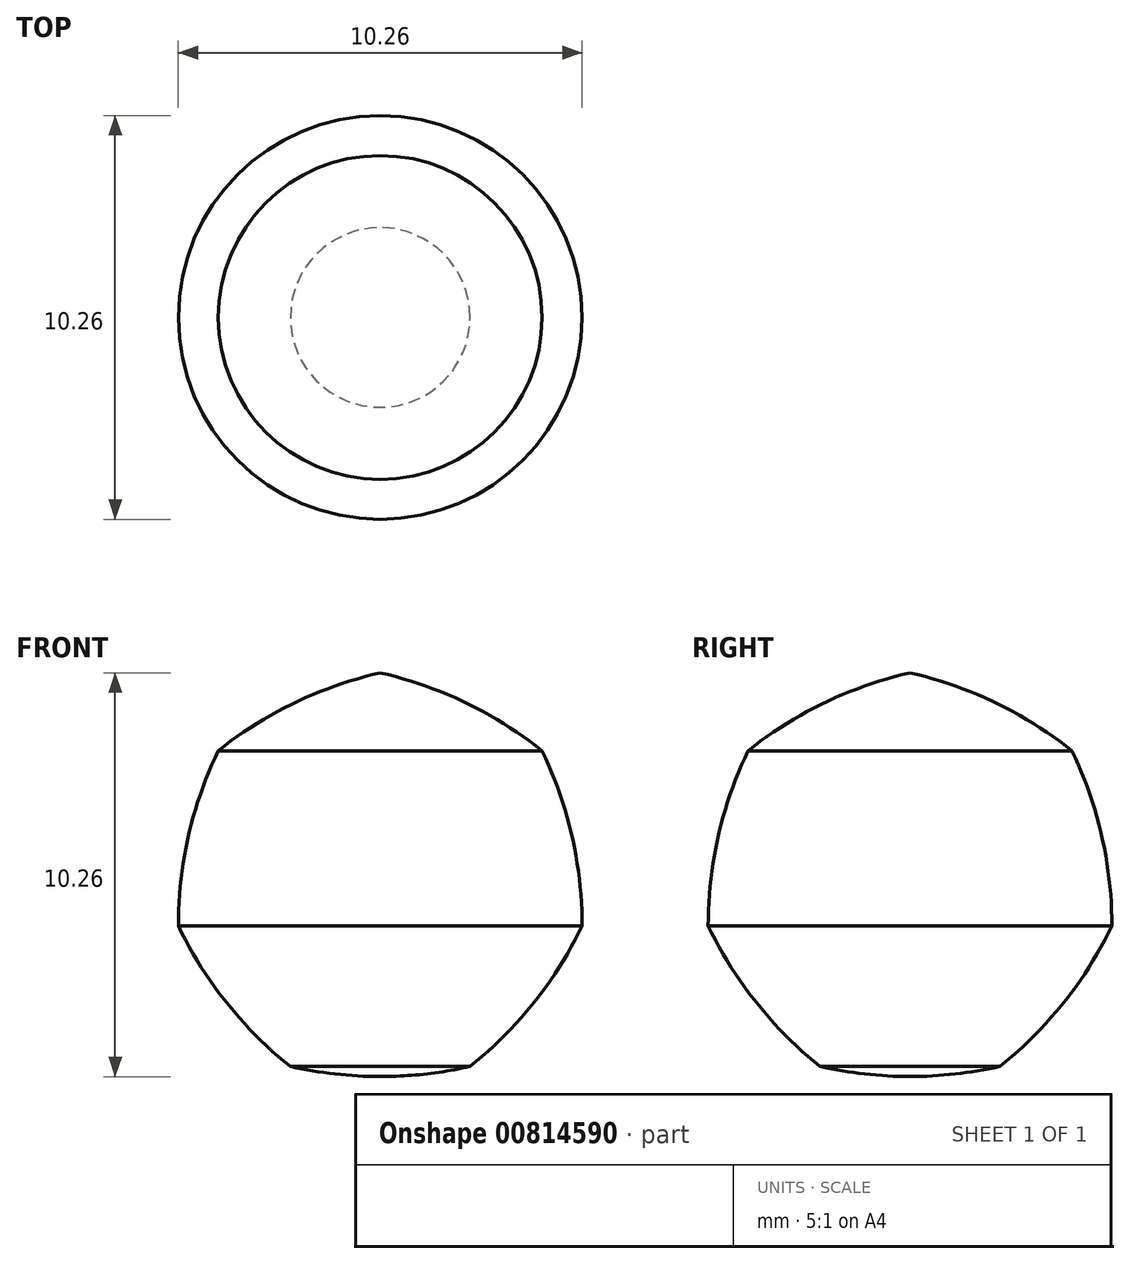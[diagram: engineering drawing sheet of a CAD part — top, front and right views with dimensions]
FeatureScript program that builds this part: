
annotation { "Feature Type Name" : "Feature", "Feature Type Description" : "" }
export const myFeature = defineFeature(function(context is Context, id is Id, definition is map)
    precondition{}
    {
        {
            var Q0;
            Q0=qCreatedBy(makeId("Front.planeOp"),FACE);
            var sketch = newSketch(context, id + "F0", { "sketchPlane" : qUnion([Q0])});
            skArc(sketch, "E0.cCircle", {"start": v(0, -4.74) * mm, "mid": v(4.74, 0) * mm, "end": v(0, 4.74) * mm, "construction": true});
            skLineSegment(sketch, "E0.0", {"start": v(2.28, -4.74) * mm, "end": v(0, -4.74) * mm});
            skLineSegment(sketch, "E0.4", {"start": v(0, 5.26) * mm, "end": v(4.11, 3.28) * mm});
            skLineSegment(sketch, "E0.5", {"start": v(4.11, 3.28) * mm, "end": v(5.13, -1.17) * mm});
            skLineSegment(sketch, "E0.6", {"start": v(5.13, -1.17) * mm, "end": v(2.28, -4.74) * mm});
            skPoint(sketch, "E0.0.midPoint", {"position": v(0, -4.74) * mm});
            skArc(sketch, "E1", {"start": v(0, -5) * mm, "mid": v(1.15, -4.93) * mm, "end": v(2.28, -4.74) * mm});
            skArc(sketch, "E2.trimOffspring", {"start": v(4.11, 3.28) * mm, "mid": v(2.17, 4.5) * mm, "end": v(0, 5.26) * mm});
            skArc(sketch, "E3.trimOffspring", {"start": v(5.13, -1.17) * mm, "mid": v(4.87, 1.11) * mm, "end": v(4.11, 3.28) * mm});
            skArc(sketch, "E4.trimOffspring", {"start": v(2.28, -4.74) * mm, "mid": v(3.9, -3.12) * mm, "end": v(5.13, -1.17) * mm});
            skLineSegment(sketch, "E5", {"start": v(0, 7.42) * mm, "end": v(0, -6.57) * mm});
            skSolve(sketch);
        }
        {
            var Q0;
            Q0 = qSketchRegion(id + "F0", true);
            var Q1;
            Q1=sQuery(id+"F0.wireOp",EDGE,"E5");
            revolve(context, id + "F1", {"surfaceOperationType" : NewSurfaceOperationType.NEW, "entities" : qUnion([Q0]), "axis" : qUnion([Q1]), "revolveType" : RevolveType.FULL});
        }
    });
